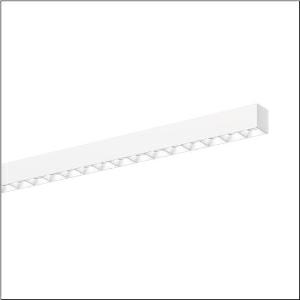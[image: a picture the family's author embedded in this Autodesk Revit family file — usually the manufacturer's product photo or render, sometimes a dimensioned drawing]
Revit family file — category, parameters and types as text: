
# Revit family: silica_r__21_51mx26db35wb_1250
name_source: partatom
category: Lighting Fixtures
units: mm (PartAtom-declared; Revit-internal decimal feet)

## family parameters
Cut with Voids When Loaded = No
Host = Face
Light Source = No
Part Type = Normal
Room Calculation Point = No
Round Connector Dimension = Use Diameter
Shared = No

## types (1)
- --- (1 x LED, 5400 lm, 31.4 W, 3000K)
    Apparent Load = 31 VA
    CIE Flux Codes = 83 98 100 100 100
    Color Rendering = 80
    Color Temperature = 3000K
    Default Elevation = 1800 mm
    Description = Silica® 21, office luminaire, primary light control with darklight reflector, of PMMA, white, CAT 2 (L<= 3000cd/m²), light emission: direct distribution, primary light characteristic: symmetric, installation type: surface-mounted, LED, rated luminous flux: 5.400lm, luminous efficacy: 172lm/W, light colour: 830, colour temperature: 3000K, with terminal, 3+2-pole, max. 2.5mm², mains connection: 220..240V, AC, 50/60Hz, rated input power: 31.4W, luminaire housing, of aluminium, traffic white (RAL 9016), length: 1.504mm, width: 53mm, height: 53mm, protection rating (complete): IP20, insulation class (complete): insulation class I (protective earthing), certification: CE, permissible operating ambient temperature: 0..+35°C, standard: EN 50419, packaging unit: 1 piece
    Height = 0 mm  [stored 0 ft]
    Lamp = 1 x LED
    Lamp Light Flux = 5400 lm
    Lamp Power = 31.4 W
    Lamp count = 1
    Length = 1504 mm
    Luminous efficacy = 172 lm/W
    Manufacturer = Siteco
    ModVariant = No
    Model = 51MX26DB35WB
    Mounting Place = Ceiling
    Mounting Type = Recessed
    Number of Poles = 1
    OnlyDefault = Yes
    Power Factor = 1
    Product Name = Silica® 21
    Product group = office luminaire | ceiling recessed
    ProductGroupID = 401
    Protection Class = Protection class I
    Protection Degree = IP 20
    RLX_Detail_Level = 1
    RLX_Emergency_Light_Flux = 0 lm
    RLX_Emergency_Type = 0
    RLX_Emergency_Type_DB = No
    RlxData = <blob elided: 41849 chars, md5=96afbd2e>
    Socket = socket
    Standby Power = 0 W
    System Light Flux = 5400 lm
    System Power = 31 W
    Type Comments = factory setting: luminous flux: 100 % | dim-lin: 254 | 360 mA
    Type Image = l_1297772.jpg
    URL = http://relux.com
    VarID = @adj_055367
    Voltage = 0 V
    Weight = 0.00 kg
    Width = 53 mm

note: [stored X ft] marks values corroborated as IEEE doubles in the binary element streams (Revit-internal decimal feet)

## geometry (parser evidence)
native form markers: Blend x4, Sweep x9
no freeform markers — native parametric forms only
